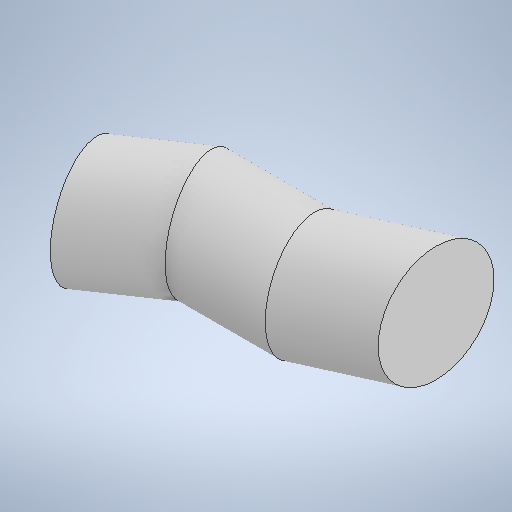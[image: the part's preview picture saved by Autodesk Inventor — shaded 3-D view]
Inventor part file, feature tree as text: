
AUTODESK INVENTOR PART (.ipt)
format: ipt  version: 2025.2 (Build 292293000, 293)  size: 226,816 bytes
history: native  units: mm
features: sketch x2, sweep x1
ambient origin geometry x8: Origin, YZ Plane, XZ Plane, XY Plane, X Axis, Y Axis, Z Axis, Center Point
bodies: Solid1 (feature_tree)
feature tree (3):
  sweep  "Sweep1"
  sketch  "Sketch1"  dims[d0=0.0mm d1=0.0mm]
  sketch  "Sketch2"
